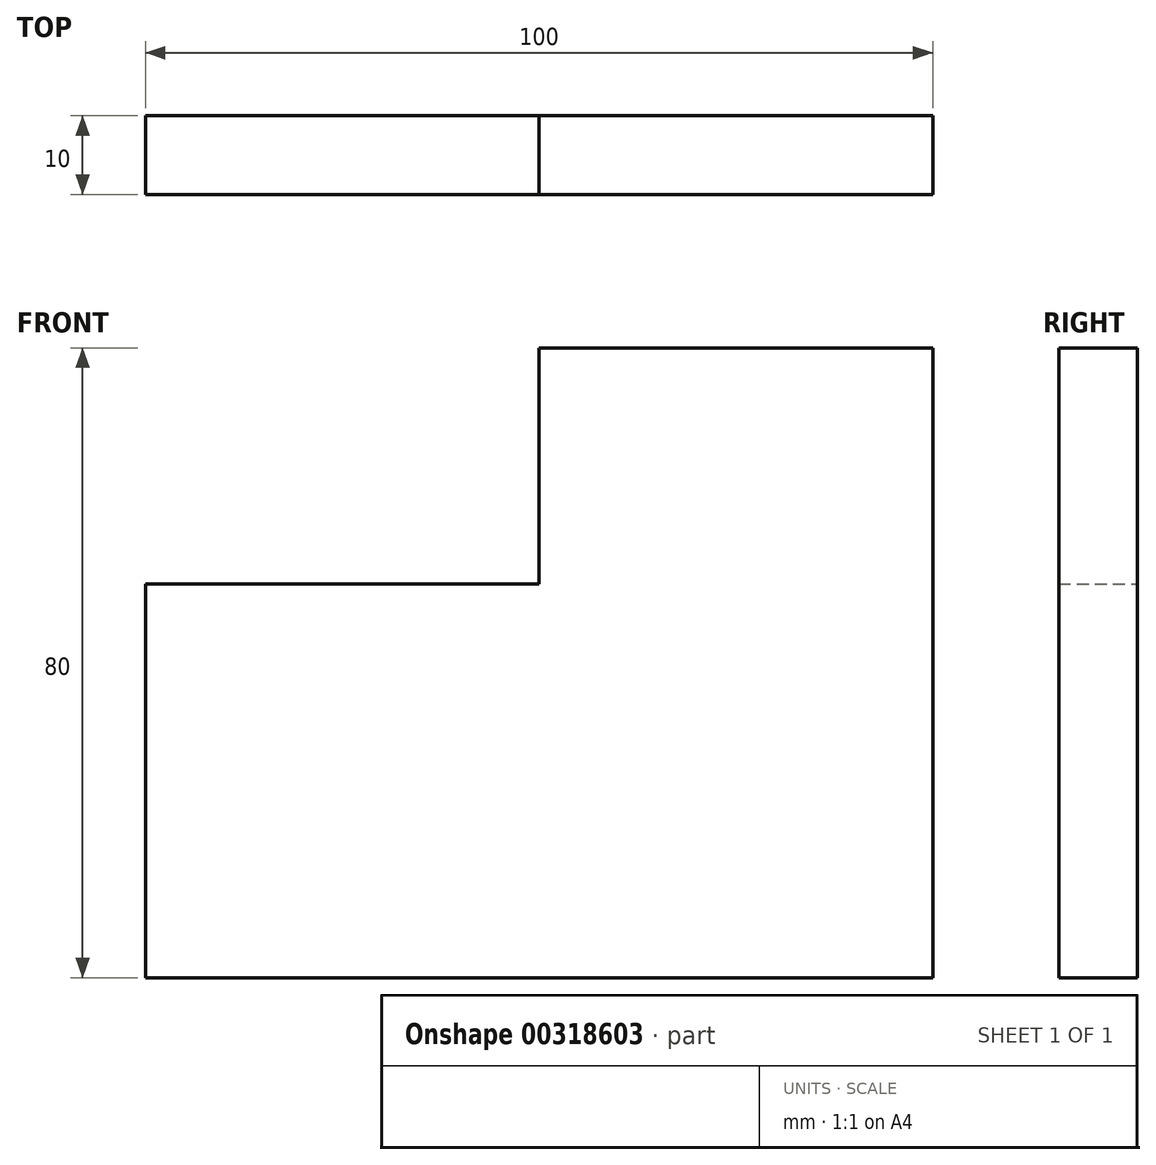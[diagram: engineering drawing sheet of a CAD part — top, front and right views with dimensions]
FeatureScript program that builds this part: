
annotation { "Feature Type Name" : "Feature", "Feature Type Description" : "" }
export const myFeature = defineFeature(function(context is Context, id is Id, definition is map)
    precondition{}
    {
        {
            var Q0;
            Q0=qCreatedBy(makeId("Front.planeOp"),FACE);
            var sketch = newSketch(context, id + "F0", { "sketchPlane" : qUnion([Q0])});
            skLineSegment(sketch, "E0", {"start": v(0, 0) * mm, "end": v(0, 80) * mm});
            skLineSegment(sketch, "E1", {"start": v(0, 80) * mm, "end": v(-50, 80) * mm});
            skLineSegment(sketch, "E2", {"start": v(-50, 80) * mm, "end": v(-50, 50) * mm});
            skLineSegment(sketch, "E3", {"start": v(-50, 50) * mm, "end": v(-100, 50) * mm});
            skLineSegment(sketch, "E4", {"start": v(-100, 50) * mm, "end": v(-100, 0) * mm});
            skLineSegment(sketch, "E5", {"start": v(-100, 0) * mm, "end": v(0, 0) * mm});
            skSolve(sketch);
        }
        {
            var Q0;
            Q0 = qSketchRegion(id + "F0", true);
            extrude(context, id + "F1", {"entities" : qUnion([Q0]), "depth" : 10 * mm});
        }
    });
